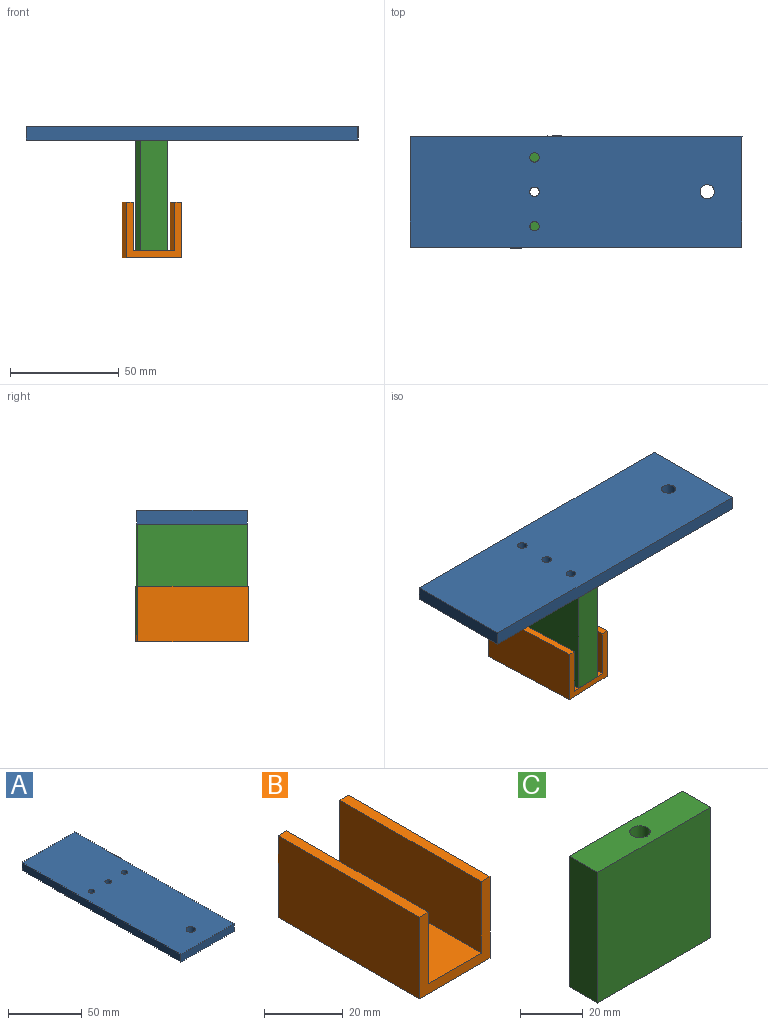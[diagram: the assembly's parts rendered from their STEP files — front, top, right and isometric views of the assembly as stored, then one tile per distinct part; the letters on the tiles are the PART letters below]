
ASSEMBLY  parts=3 mates=3
PART A: 10 faces, bbox 50.8x152.4x6.4 mm
  f0: plane 50.8x6.35mm, normal (0,1,0), area 322.6mm2, adj f1,f7,f8,f9
  f1: plane 152.4x6.35mm, normal (-1,0,0), area 967.7mm2, adj f0,f2,f8,f9
  f2: plane 50.8x6.35mm, normal (0,-1,0), area 322.6mm2, adj f1,f7,f8,f9
  f3: cylinder r=2.17mm len=6.35mm, axis (0,0,-1), area 86.6mm2, adj f8,f9
  f4: cylinder r=2.17mm len=6.35mm, axis (0,0,-1), area 86.6mm2, adj f8,f9
  f5: cylinder r=2.17mm len=6.35mm, axis (0,0,-1), area 86.6mm2, adj f8,f9
  f6: cylinder r=3.26mm len=6.53mm, axis (0,0,-1), area 130.2mm2, adj f8,f9
  f7: plane 152.4x6.35mm, normal (1,0,0), area 967.7mm2, adj f0,f2,f8,f9
  f8: plane 152.4x50.8mm, normal (0,0,1), area 7664mm2, adj f0,f1,f2,f3,f4,f5,f6,f7
  f9: plane 152.4x50.8mm, normal (0,0,-1), area 7664mm2, adj f0,f1,f2,f3,f4,f5,f6,f7
PART B: 11 faces, bbox 25.4x50.8x25.4 mm
  f0: plane 50.8x3.18mm, normal (0,0,1), area 161.3mm2, adj f1,f7,f8,f9
  f1: plane 50.8x25.4mm, normal (-1,0,0), area 1290.3mm2, adj f0,f2,f8,f9
  f2: plane 50.8x25.4mm, normal (0,0,-1), area 1258.7mm2, adj f1,f3,f8,f9,f10
  f3: plane 50.8x25.4mm, normal (1,0,0), area 1290.3mm2, adj f2,f4,f8,f9
  f4: plane 50.8x3.18mm, normal (0,0,1), area 161.3mm2, adj f3,f5,f8,f9
  f5: plane 50.8x22.23mm, normal (-1,0,0), area 1129mm2, adj f4,f6,f8,f9
  f6: plane 50.8x19.05mm, normal (0,0,1), area 936.1mm2, adj f5,f7,f8,f9,f10
  f7: plane 50.8x22.23mm, normal (1,0,0), area 1129mm2, adj f0,f6,f8,f9
  f8: plane 25.4x25.4mm, normal (0,-1,0), area 221.8mm2, adj f0,f1,f2,f3,f4,f5,f6,f7
  f9: plane 25.4x25.4mm, normal (0,1,0), area 221.8mm2, adj f0,f1,f2,f3,f4,f5,f6,f7
  f10: cylinder r=3.17mm len=6.35mm, axis (0,0,-1), area 63.3mm2, adj f2,f6
PART C: 11 faces, bbox 50.8x12.7x50.8 mm
  f0: plane 50.8x50.8mm, normal (0,1,0), area 2580.6mm2, adj f1,f3,f4,f5
  f1: plane 50.8x12.7mm, normal (-1,0,0), area 645.2mm2, adj f0,f2,f4,f5
  f2: plane 50.8x50.8mm, normal (0,-1,0), area 2580.6mm2, adj f1,f3,f4,f5
  f3: plane 50.8x12.7mm, normal (1,0,0), area 645.2mm2, adj f0,f2,f4,f5
  f4: plane 50.8x12.7mm, normal (0,0,1), area 611.7mm2, adj f0,f1,f2,f3,f8
  f5: plane 50.8x12.7mm, normal (0,0,-1), area 544.8mm2, adj f0,f1,f2,f3,f6,f8,f9
  f6: cylinder r=3.26mm len=19.05mm, axis (0,0,-1), area 390.7mm2, adj f5,f7
  f7: plane 6.53x6.53mm, normal (0,0,-1), area 33.5mm2, adj f6
  f8: cylinder r=3.26mm len=50.8mm, axis (0,0,-1), area 1041.8mm2, adj f4,f5
  f9: cylinder r=3.26mm len=19.05mm, axis (0,0,-1), area 390.7mm2, adj f5,f10
  f10: plane 6.53x6.53mm, normal (0,0,-1), area 33.5mm2, adj f9
PLACE A rot(axis=(0,0,1),90deg) t=(-15.34,67.32,142.38)mm
PLACE B rot(axis=(0,0,1),2.3deg) t=(-22.49,42.82,101.1)mm
PLACE C rot(axis=(-0.72,0.69,0),180deg) t=(-29.54,19.69,142.38)mm
MATE pin_slot C.f9 <-> A.f5  axis (0,0,1) through (-22.11,33.21,142.38)mm
MATE pin_slot C.f6 <-> A.f3  axis (0,0,1) through (-20.84,1.66,142.38)mm
MATE pin_slot B.f10 <-> C.f8  axis (0,0,1) through (-21.47,17.44,91.58)mm
